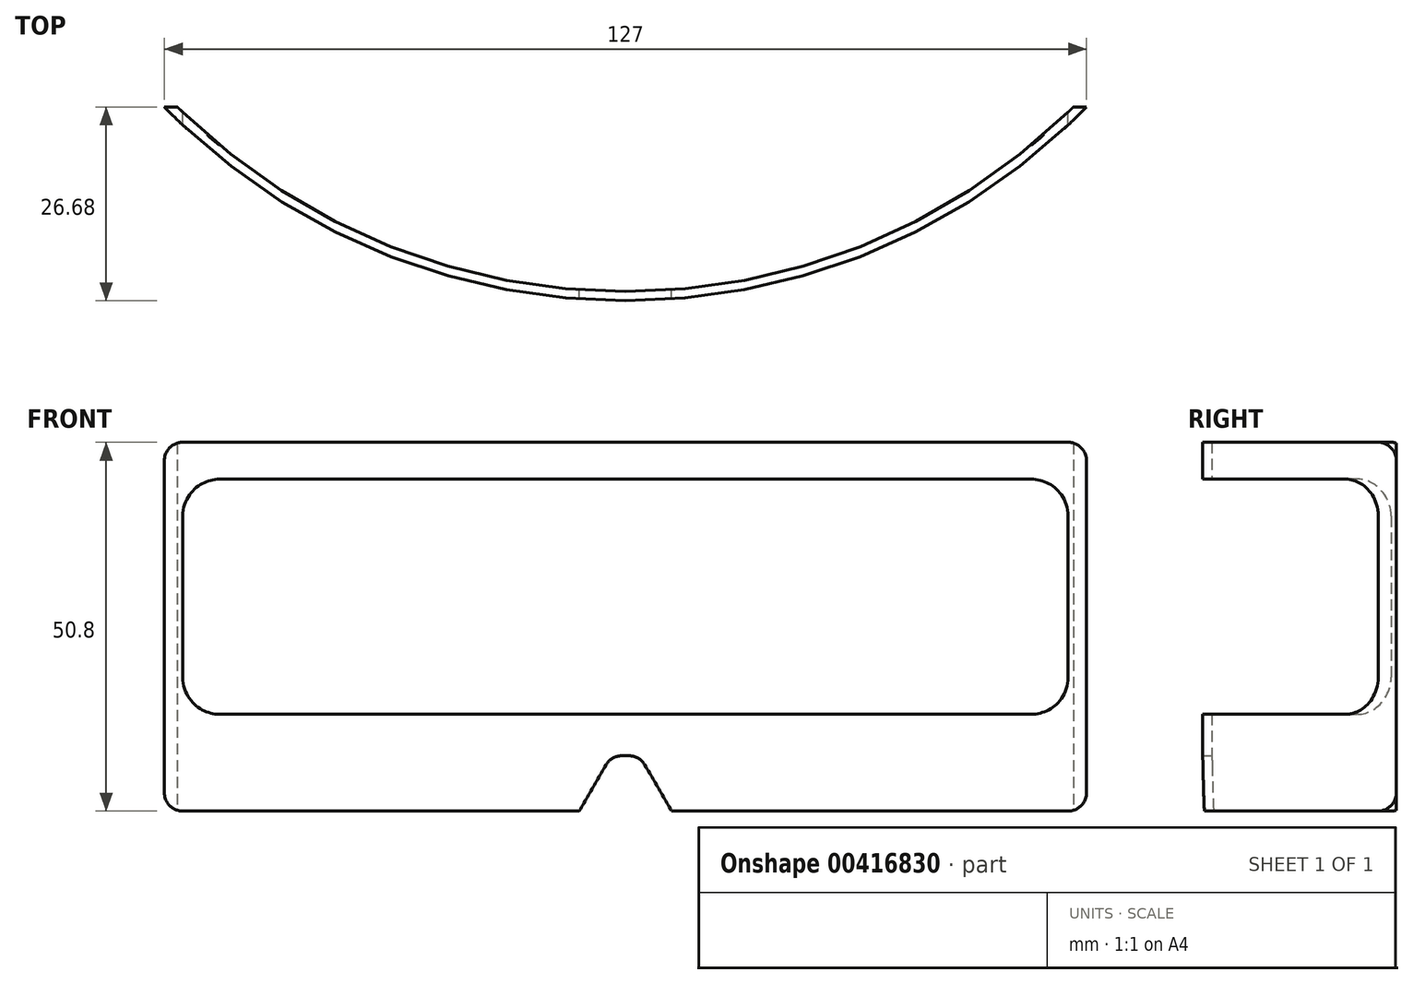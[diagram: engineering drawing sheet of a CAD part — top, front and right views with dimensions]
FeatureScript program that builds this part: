
annotation { "Feature Type Name" : "Feature", "Feature Type Description" : "" }
export const myFeature = defineFeature(function(context is Context, id is Id, definition is map)
    precondition{}
    {
        {
            var Q0;
            Q0=qCreatedBy(makeId("Top.planeOp"),FACE);
            var sketch = newSketch(context, id + "F0", { "sketchPlane" : qUnion([Q0])});
            skArc(sketch, "E0", {"start": v(-63.5, -62.22) * mm, "mid": v(0, -88.9) * mm, "end": v(63.5, -62.22) * mm});
            skLineSegment(sketch, "E1", {"start": v(-63.5, -62.22) * mm, "end": v(-61.7, -62.22) * mm});
            skArc(sketch, "E2.0", {"start": v(-61.7, -62.22) * mm, "mid": v(0, -87.63) * mm, "end": v(61.7, -62.22) * mm});
            skLineSegment(sketch, "E3", {"start": v(63.5, -62.22) * mm, "end": v(61.7, -62.22) * mm});
            skLineSegment(sketch, "E4.trimOffspring", {"start": v(61.7, -62.22) * mm, "end": v(63.5, -62.22) * mm});
            skLineSegment(sketch, "E5", {"start": v(0, 0) * mm, "end": v(0, -127) * mm, "construction": true});
            skLineSegment(sketch, "E6", {"start": v(-68.2, -88.9) * mm, "end": v(185.8, -88.9) * mm, "construction": true});
            skLineSegment(sketch, "E7", {"start": v(-63.5, -62.22) * mm, "end": v(63.5, -62.22) * mm, "construction": true});
            skSolve(sketch);
        }
        {
            var Q0;
            Q0=makeQuery(id+"F0.imprint","IMPRINT",FACE,{"disambiguationData":[TD([[makeQuery(id+"F0.imprint","IMPRINT",EDGE,{"derivedFrom":sQuery(id+"F0.wireOp",EDGE,"E0")}),1.0]])]});
            extrude(context, id + "F1", {"entities" : qUnion([Q0]), "depth" : 63.5 * mm, "offsetDistance" : 25.4 * mm});
        }
        {
            var Q0;
            Q0=qCreatedBy(makeId("Front.planeOp"),FACE);
            var sketch = newSketch(context, id + "F2", { "sketchPlane" : qUnion([Q0])});
            skLineSegment(sketch, "E8", {"start": v(0, 0) * mm, "end": v(0, 87.03) * mm, "construction": true});
            skLineSegment(sketch, "E9", {"start": v(-84.88, 0) * mm, "end": v(109.53, 0) * mm, "construction": true});
            skLineSegment(sketch, "E10.bottom", {"start": v(-60.96, 50.8) * mm, "end": v(60.96, 50.8) * mm});
            skLineSegment(sketch, "E10.top", {"start": v(-60.96, 0) * mm, "end": v(60.96, 0) * mm});
            skLineSegment(sketch, "E10.left", {"start": v(-63.5, 48.26) * mm, "end": v(-63.5, 2.54) * mm});
            skLineSegment(sketch, "E10.right", {"start": v(63.5, 48.26) * mm, "end": v(63.5, 2.54) * mm});
            skLineSegment(sketch, "E11.bottom", {"start": v(-55.88, 45.72) * mm, "end": v(55.88, 45.72) * mm});
            skLineSegment(sketch, "E11.top", {"start": v(-55.88, 13.33) * mm, "end": v(55.88, 13.33) * mm});
            skLineSegment(sketch, "E11.left", {"start": v(-60.96, 40.64) * mm, "end": v(-60.96, 18.41) * mm});
            skLineSegment(sketch, "E11.right", {"start": v(60.96, 40.64) * mm, "end": v(60.96, 18.41) * mm});
            skPoint(sketch, "E12.visualSharp", {"position": v(-63.5, 50.8) * mm});
            skArc(sketch, "E12.filletArc", {"start": v(-60.96, 50.8) * mm, "mid": v(-62.76, 50.06) * mm, "end": v(-63.5, 48.26) * mm});
            skPoint(sketch, "E13.visualSharp", {"position": v(-60.96, 45.72) * mm});
            skArc(sketch, "E13.filletArc", {"start": v(-55.88, 45.72) * mm, "mid": v(-59.47, 44.23) * mm, "end": v(-60.96, 40.64) * mm});
            skPoint(sketch, "E14.visualSharp", {"position": v(-60.96, 13.33) * mm});
            skArc(sketch, "E14.filletArc", {"start": v(-60.96, 18.41) * mm, "mid": v(-59.47, 14.82) * mm, "end": v(-55.88, 13.33) * mm});
            skPoint(sketch, "E15.visualSharp", {"position": v(-63.5, 0) * mm});
            skArc(sketch, "E15.filletArc", {"start": v(-63.5, 2.54) * mm, "mid": v(-62.76, 0.74) * mm, "end": v(-60.96, 0) * mm});
            skPoint(sketch, "E16.visualSharp", {"position": v(63.5, 50.8) * mm});
            skArc(sketch, "E16.filletArc", {"start": v(63.5, 48.26) * mm, "mid": v(62.76, 50.06) * mm, "end": v(60.96, 50.8) * mm});
            skPoint(sketch, "E17.visualSharp", {"position": v(60.96, 45.72) * mm});
            skArc(sketch, "E17.filletArc", {"start": v(60.96, 40.64) * mm, "mid": v(59.47, 44.23) * mm, "end": v(55.88, 45.72) * mm});
            skPoint(sketch, "E18.visualSharp", {"position": v(60.96, 13.33) * mm});
            skArc(sketch, "E18.filletArc", {"start": v(55.88, 13.33) * mm, "mid": v(59.47, 14.82) * mm, "end": v(60.96, 18.41) * mm});
            skPoint(sketch, "E19.visualSharp", {"position": v(63.5, 0) * mm});
            skArc(sketch, "E19.filletArc", {"start": v(60.96, 0) * mm, "mid": v(62.76, 0.74) * mm, "end": v(63.5, 2.54) * mm});
            skLineSegment(sketch, "E20", {"start": v(-6.35, 0) * mm, "end": v(6.35, 0) * mm});
            skLineSegment(sketch, "E21", {"start": v(6.35, 0) * mm, "end": v(2.68, 6.35) * mm});
            skLineSegment(sketch, "E22", {"start": v(0.48, 7.62) * mm, "end": v(-0.48, 7.62) * mm});
            skLineSegment(sketch, "E23", {"start": v(-2.68, 6.35) * mm, "end": v(-6.35, 0) * mm});
            skPoint(sketch, "E24.visualSharp", {"position": v(-1.95, 7.62) * mm});
            skArc(sketch, "E24.filletArc", {"start": v(-0.48, 7.62) * mm, "mid": v(-1.75, 7.28) * mm, "end": v(-2.68, 6.35) * mm});
            skPoint(sketch, "E25.visualSharp", {"position": v(1.95, 7.62) * mm});
            skArc(sketch, "E25.filletArc", {"start": v(2.68, 6.35) * mm, "mid": v(1.75, 7.28) * mm, "end": v(0.48, 7.62) * mm});
            skLineSegment(sketch, "E26.bottom", {"start": v(63.5, 0) * mm, "end": v(-63.5, 0) * mm});
            skLineSegment(sketch, "E26.top", {"start": v(63.5, 63.5) * mm, "end": v(-63.5, 63.5) * mm});
            skLineSegment(sketch, "E26.left", {"start": v(63.5, 0) * mm, "end": v(63.5, 63.5) * mm});
            skLineSegment(sketch, "E26.right", {"start": v(-63.5, 0) * mm, "end": v(-63.5, 63.5) * mm});
            skSolve(sketch);
        }
        {
            var Q0;
            Q0=makeQuery(id+"F2.imprint","IMPRINT",FACE,{"disambiguationData":[TD([[makeQuery(id+"F2.imprint","IMPRINT",EDGE,{"derivedFrom":sQuery(id+"F2.wireOp",EDGE,"E10.bottom")}),1.0]])]});
            var Q1;
            Q1=makeQuery(id+"F2.imprint","IMPRINT",FACE,{"disambiguationData":[TD([[makeQuery(id+"F2.imprint","IMPRINT",EDGE,{"derivedFrom":sQuery(id+"F2.wireOp",EDGE,"E11.bottom")}),-1.0]])]});
            var Q2;
            {var subQ0=sQuery(id+"F2.wireOp",EDGE,"E19.filletArc");Q2=makeQuery(id+"F2.imprint","IMPRINT",FACE,{"disambiguationData":[TD([[makeQuery(id+"F2.imprint","IMPRINT",EDGE,{"derivedFrom":subQ0}),-1.0]])]});}
            var Q3;
            {var subQ1=sQuery(id+"F2.wireOp",EDGE,"E21");Q3=makeQuery(id+"F2.imprint","IMPRINT",FACE,{"disambiguationData":[TD([[makeQuery(id+"F2.imprint","IMPRINT",EDGE,{"derivedFrom":subQ1}),1.0]])]});}
            var Q4;
            {var subQ0=sQuery(id+"F2.wireOp",EDGE,"E15.filletArc");Q4=makeQuery(id+"F2.imprint","IMPRINT",FACE,{"disambiguationData":[TD([[makeQuery(id+"F2.imprint","IMPRINT",EDGE,{"derivedFrom":subQ0}),-1.0]])]});}
            extrude(context, id + "F3", {"entities" : qUnion([Q0, Q1, Q2, Q3, Q4]), "operationType" : NewBodyOperationType.REMOVE, "depth" : 127 * mm, "offsetDistance" : 25.4 * mm});
        }
    });
